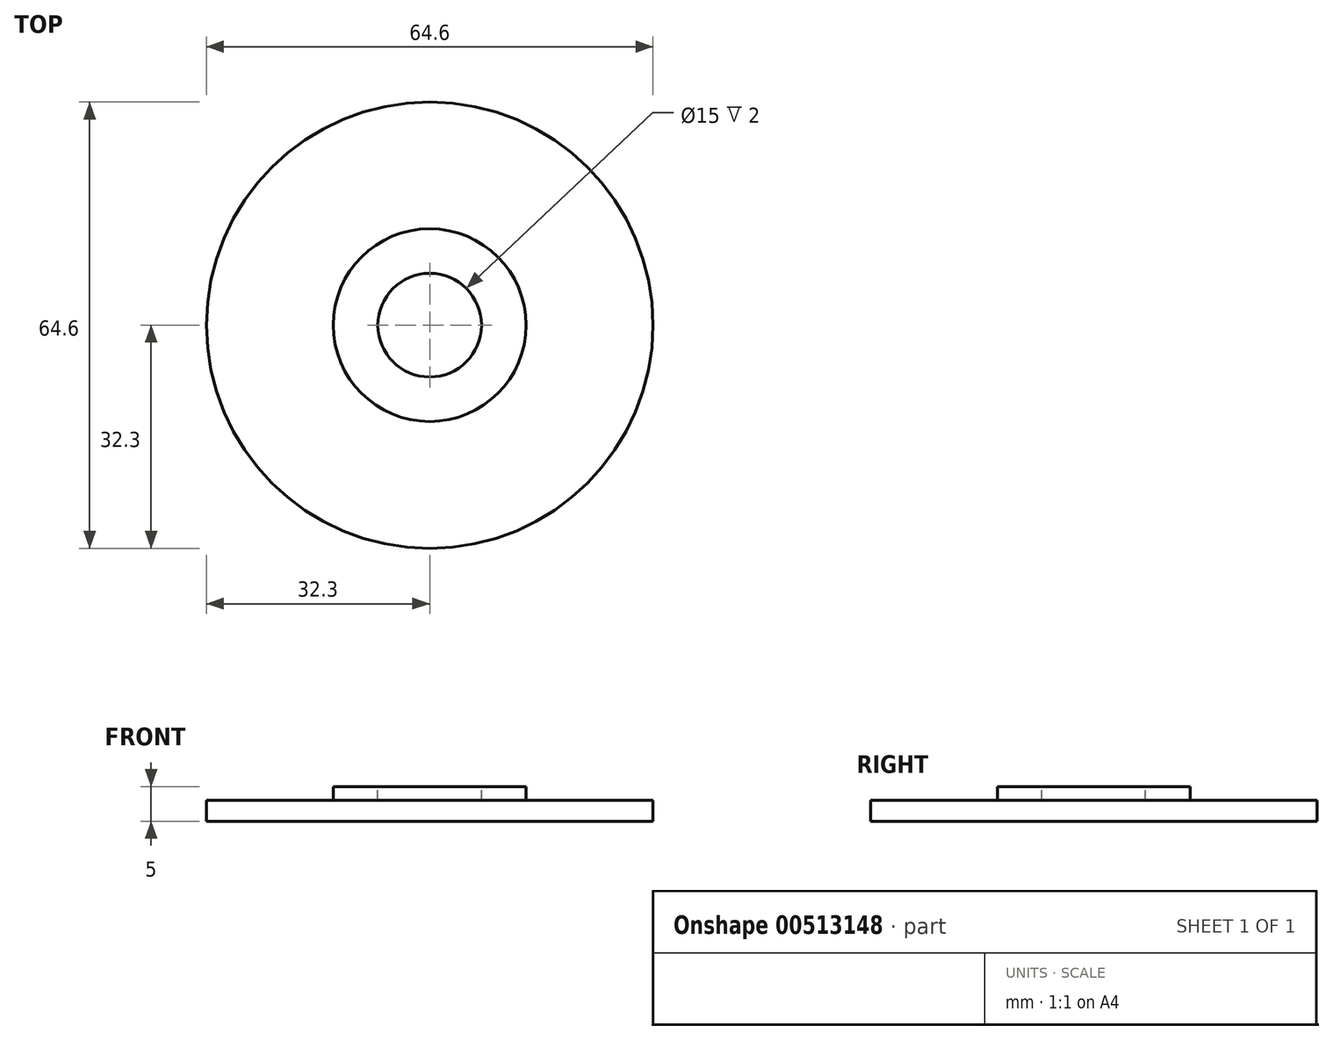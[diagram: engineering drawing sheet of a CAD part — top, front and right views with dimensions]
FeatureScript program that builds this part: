
annotation { "Feature Type Name" : "Feature", "Feature Type Description" : "" }
export const myFeature = defineFeature(function(context is Context, id is Id, definition is map)
    precondition{}
    {
        {
            var Q0;
            Q0=qCreatedBy(makeId("Top.planeOp"),FACE);
            var sketch = newSketch(context, id + "F0", { "sketchPlane" : qUnion([Q0])});
            skCircle(sketch, "E0", {"center": v(0, 0) * mm, "radius": 32.3 * mm});
            skSolve(sketch);
        }
        {
            var Q0;
            Q0 = qSketchRegion(id + "F0", true);
            extrude(context, id + "F1", {"entities" : qUnion([Q0]), "depth" : 3 * mm});
        }
        {
            var Q0;
            Q0=qCreatedBy(makeId("Top.planeOp"),FACE);
            var sketch = newSketch(context, id + "F2", { "sketchPlane" : qUnion([Q0])});
            skCircle(sketch, "E1", {"center": v(0, 0) * mm, "radius": 13.95 * mm});
            skSolve(sketch);
        }
        {
            var Q0;
            Q0 = qSketchRegion(id + "F2", true);
            extrude(context, id + "F3", {"entities" : qUnion([Q0]), "operationType" : NewBodyOperationType.ADD, "depth" : 5 * mm});
        }
        {
            var Q0;
            Q0=makeQuery(id+"F3.opExtrude","CAP_FACE",FACE,{"disambiguationData":[OSD([sQuery(id+"F2.wireOp",EDGE,"E1")])],"isStart":false});
            var sketch = newSketch(context, id + "F4", { "sketchPlane" : qUnion([Q0])});
            skCircle(sketch, "E2", {"center": v(0, 0) * mm, "radius": 7.5 * mm});
            skSolve(sketch);
        }
        {
            var Q0;
            Q0=makeQuery(id+"F4.imprint","IMPRINT",FACE,{"disambiguationData":[TD([[makeQuery(id+"F4.imprint","IMPRINT",EDGE,{"derivedFrom":sQuery(id+"F4.wireOp",EDGE,"E2")}),1.0]])]});
            extrude(context, id + "F5", {"entities" : qUnion([Q0]), "operationType" : NewBodyOperationType.REMOVE, "oppositeDirection" : true, "depth" : 2 * mm});
        }
    });
